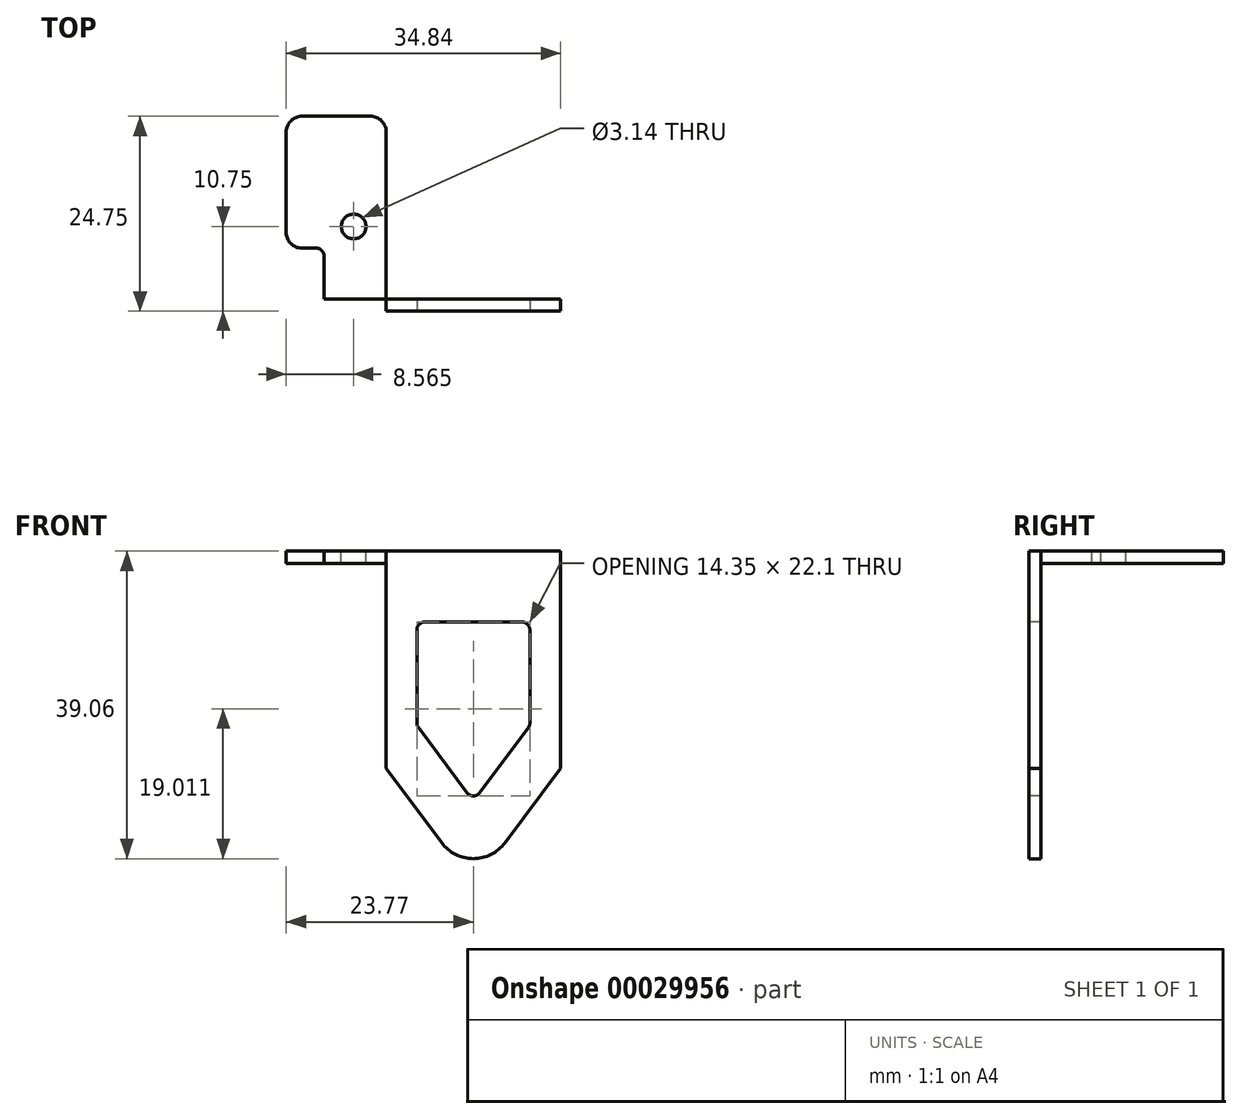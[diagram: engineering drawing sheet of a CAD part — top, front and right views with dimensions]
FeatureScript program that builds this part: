
annotation { "Feature Type Name" : "Feature", "Feature Type Description" : "" }
export const myFeature = defineFeature(function(context is Context, id is Id, definition is map)
    precondition{}
    {
        {
            var Q0;
            Q0=qCreatedBy(makeId("Top.planeOp"),FACE);
            var sketch = newSketch(context, id + "F0", { "sketchPlane" : qUnion([Q0])});
            skCircle(sketch, "E0", {"center": v(-15.2, 0) * mm, "radius": 1.57 * mm});
            skLineSegment(sketch, "E1", {"start": v(-15.2, 0) * mm, "end": v(0, 0) * mm, "construction": true});
            skLineSegment(sketch, "E2", {"start": v(0, 0) * mm, "end": v(15.2, 0) * mm, "construction": true});
            skLineSegment(sketch, "E3.bottom", {"start": v(-21.77, 14) * mm, "end": v(-13.07, 14) * mm});
            skLineSegment(sketch, "E3.top", {"start": v(-18.97, -10.75) * mm, "end": v(-11.07, -10.75) * mm});
            skLineSegment(sketch, "E3.left", {"start": v(-23.77, 12) * mm, "end": v(-23.77, -0.75) * mm});
            skLineSegment(sketch, "E3.right", {"start": v(-11.07, 12) * mm, "end": v(-11.07, -10.75) * mm});
            skLineSegment(sketch, "E4", {"start": v(-21.77, -2.75) * mm, "end": v(-19.97, -2.75) * mm});
            skLineSegment(sketch, "E5", {"start": v(-18.97, -3.75) * mm, "end": v(-18.97, -10.75) * mm});
            skPoint(sketch, "E6.visualSharp", {"position": v(-23.77, 14) * mm});
            skArc(sketch, "E6.filletArc", {"start": v(-21.77, 14) * mm, "mid": v(-23.18, 13.41) * mm, "end": v(-23.77, 12) * mm});
            skPoint(sketch, "E7.visualSharp", {"position": v(-11.07, 14) * mm});
            skArc(sketch, "E7.filletArc", {"start": v(-11.07, 12) * mm, "mid": v(-11.66, 13.41) * mm, "end": v(-13.07, 14) * mm});
            skPoint(sketch, "E8.visualSharp", {"position": v(-23.77, -2.75) * mm});
            skArc(sketch, "E8.filletArc", {"start": v(-23.77, -0.75) * mm, "mid": v(-23.18, -2.16) * mm, "end": v(-21.77, -2.75) * mm});
            skPoint(sketch, "E9.visualSharp", {"position": v(-18.97, -2.75) * mm});
            skArc(sketch, "E9.filletArc", {"start": v(-18.97, -3.75) * mm, "mid": v(-19.26, -3.04) * mm, "end": v(-19.97, -2.75) * mm});
            skLineSegment(sketch, "E10", {"start": v(0, 0) * mm, "end": v(0, -9.93) * mm, "construction": true});
            skArc(sketch, "E11.MirrorCS", {"start": v(18.97, -3.75) * mm, "mid": v(19.26, -3.04) * mm, "end": v(19.97, -2.75) * mm});
            skArc(sketch, "E12.MirrorCS", {"start": v(23.77, -0.75) * mm, "mid": v(23.18, -2.16) * mm, "end": v(21.77, -2.75) * mm});
            skCircle(sketch, "E13.MirrorC", {"center": v(15.2, 0) * mm, "radius": 1.57 * mm});
            skPoint(sketch, "E14.MirrorP", {"position": v(11.07, 14) * mm});
            skPoint(sketch, "E15.MirrorP", {"position": v(18.97, -2.75) * mm});
            skLineSegment(sketch, "E16.MirrorCS", {"start": v(18.97, -10.75) * mm, "end": v(11.07, -10.75) * mm});
            skLineSegment(sketch, "E17.MirrorCS", {"start": v(23.77, 12) * mm, "end": v(23.77, -0.75) * mm});
            skLineSegment(sketch, "E18.MirrorCS", {"start": v(21.77, -2.75) * mm, "end": v(19.97, -2.75) * mm});
            skLineSegment(sketch, "E19.MirrorCS", {"start": v(11.07, 12) * mm, "end": v(11.07, -10.75) * mm});
            skPoint(sketch, "E20.MirrorP", {"position": v(23.77, -2.75) * mm});
            skPoint(sketch, "E21.MirrorP", {"position": v(23.77, 14) * mm});
            skLineSegment(sketch, "E22.MirrorCS", {"start": v(18.97, -3.75) * mm, "end": v(18.97, -10.75) * mm});
            skArc(sketch, "E23.MirrorCS", {"start": v(21.77, 14) * mm, "mid": v(23.18, 13.41) * mm, "end": v(23.77, 12) * mm});
            skArc(sketch, "E24.MirrorCS", {"start": v(11.07, 12) * mm, "mid": v(11.66, 13.41) * mm, "end": v(13.07, 14) * mm});
            skLineSegment(sketch, "E25.MirrorCS", {"start": v(21.77, 14) * mm, "end": v(13.07, 14) * mm});
            skLineSegment(sketch, "E26.bottom", {"start": v(-18.97, -10.75) * mm, "end": v(18.97, -10.75) * mm});
            skLineSegment(sketch, "E26.top", {"start": v(-18.97, -9.2) * mm, "end": v(18.97, -9.2) * mm});
            skLineSegment(sketch, "E26.left", {"start": v(-18.97, -10.75) * mm, "end": v(-18.97, -9.2) * mm});
            skLineSegment(sketch, "E26.right", {"start": v(18.97, -10.75) * mm, "end": v(18.97, -9.2) * mm});
            skSolve(sketch);
        }
        {
            var Q0;
            Q0=makeQuery(id+"F0.imprint","IMPRINT",FACE,{"disambiguationData":[TD([[makeQuery(id+"F0.imprint","IMPRINT",EDGE,{"derivedFrom":sQuery(id+"F0.wireOp",EDGE,"E0")}),-1.0]])]});
            var Q1;
            Q1=makeQuery(id+"F0.imprint","IMPRINT",FACE,{"disambiguationData":[TD([[makeQuery(id+"F0.imprint","IMPRINT",EDGE,{"derivedFrom":sQuery(id+"F0.wireOp",EDGE,"E11.MirrorCS")}),1.0]])]});
            var Q2;
            {var subQ0=sQuery(id+"F0.wireOp",EDGE,"E26.left");Q2=makeQuery(id+"F0.imprint","IMPRINT",FACE,{"disambiguationData":[TD([[makeQuery(id+"F0.imprint","IMPRINT",EDGE,{"derivedFrom":subQ0}),-1.0]])]});}
            var Q3;
            {var subQ0=sQuery(id+"F0.wireOp",EDGE,"E26.right");Q3=makeQuery(id+"F0.imprint","IMPRINT",FACE,{"disambiguationData":[TD([[makeQuery(id+"F0.imprint","IMPRINT",EDGE,{"derivedFrom":subQ0}),1.0]])]});}
            extrude(context, id + "F1", {"entities" : qUnion([Q0, Q1, Q2, Q3]), "oppositeDirection" : true, "depth" : 1.55 * mm});
        }
        {
            var Q0;
            {var subQ0=sQuery(id+"F0.wireOp",EDGE,"E26.left");Q0=makeQuery(id+"F0.imprint","IMPRINT",FACE,{"disambiguationData":[TD([[makeQuery(id+"F0.imprint","IMPRINT",EDGE,{"derivedFrom":subQ0}),-1.0]])]});}
            var Q1;
            {var subQ3=sQuery(id+"F0.wireOp",EDGE,"E3.right");var subQ5=sQuery(id+"F0.wireOp",EDGE,"E26.bottom");var subQ7=makeQuery(id+"F0.imprint","INTERSECT",VERTEX,{"derivedFrom":[subQ3,subQ5]});Q1=makeQuery(id+"F0.imprint","IMPRINT",FACE,{"disambiguationData":[TD([[makeQuery(id+"F0.imprint","IMPRINT",EDGE,{"disambiguationData":[TD([[subQ7,1.0]])],"derivedFrom":subQ3}),1.0]])]});}
            var Q2;
            {var subQ0=sQuery(id+"F0.wireOp",EDGE,"E26.right");Q2=makeQuery(id+"F0.imprint","IMPRINT",FACE,{"disambiguationData":[TD([[makeQuery(id+"F0.imprint","IMPRINT",EDGE,{"derivedFrom":subQ0}),1.0]])]});}
            extrude(context, id + "F2", {"entities" : qUnion([Q0, Q1, Q2]), "operationType" : NewBodyOperationType.ADD, "oppositeDirection" : true, "depth" : 39.06 * mm});
        }
        {
            var Q0;
            {var subQ0=sQuery(id+"F0.wireOp",EDGE,"E26.bottom");Q0=makeQuery(id+"F2.boolean.opBoolean","MERGE",FACE,{"derivedFrom":[makeQuery(id+"F1.opExtrude","SWEPT_FACE",FACE,{"disambiguationData":[OSD([subQ0]),TDD([makeQuery(id+"F0.imprint","IMPRINT",EDGE,{"disambiguationData":[TD([[makeQuery(id+"F0.imprint","INTERSECT",VERTEX,{"derivedFrom":[sQuery(id+"F0.wireOp",EDGE,"E3.right"),subQ0]}),1.0]])],"derivedFrom":subQ0})])]}),makeQuery(id+"F1.opExtrude","SWEPT_FACE",FACE,{"disambiguationData":[OSD([subQ0]),TDD([makeQuery(id+"F0.imprint","IMPRINT",EDGE,{"disambiguationData":[TD([[makeQuery(id+"F0.imprint","INTERSECT",VERTEX,{"derivedFrom":[sQuery(id+"F0.wireOp",EDGE,"E19.MirrorCS"),subQ0]}),-1.0]])],"derivedFrom":subQ0})])]}),makeQuery(id+"F2.opExtrude","SWEPT_FACE",FACE,{"disambiguationData":[OSD([subQ0])]})]});}
            var sketch = newSketch(context, id + "F3", { "sketchPlane" : qUnion([Q0])});
            skLineSegment(sketch, "E27", {"start": v(-18.97, -17) * mm, "end": v(18.97, -17) * mm, "construction": true});
            skLineSegment(sketch, "E28", {"start": v(-18.97, -17) * mm, "end": v(-4, -37.05) * mm});
            skLineSegment(sketch, "E29", {"start": v(18.97, -17) * mm, "end": v(4, -37.05) * mm});
            skArc(sketch, "E30", {"start": v(-4, -37.05) * mm, "mid": v(0, -39.06) * mm, "end": v(4, -37.05) * mm});
            skLineSegment(sketch, "E31", {"start": v(-18.97, -17) * mm, "end": v(-18.97, -40.94) * mm});
            skLineSegment(sketch, "E32", {"start": v(-18.97, -40.94) * mm, "end": v(18.97, -40.94) * mm});
            skLineSegment(sketch, "E33", {"start": v(18.97, -40.94) * mm, "end": v(18.97, -17) * mm});
            skLineSegment(sketch, "E34", {"start": v(-6.18, -9) * mm, "end": v(6.18, -9) * mm});
            skLineSegment(sketch, "E35", {"start": v(7.18, -10) * mm, "end": v(7.18, -21.82) * mm});
            skLineSegment(sketch, "E36", {"start": v(6.98, -22.42) * mm, "end": v(0.8, -30.7) * mm});
            skLineSegment(sketch, "E37", {"start": v(-0.8, -30.7) * mm, "end": v(-6.98, -22.42) * mm});
            skLineSegment(sketch, "E38", {"start": v(-7.18, -21.82) * mm, "end": v(-7.18, -10) * mm});
            skPoint(sketch, "E39.visualSharp", {"position": v(0, -31.77) * mm});
            skArc(sketch, "E39.filletArc", {"start": v(-0.8, -30.7) * mm, "mid": v(0, -31.1) * mm, "end": v(0.8, -30.7) * mm});
            skPoint(sketch, "E40.visualSharp", {"position": v(-7.18, -22.15) * mm});
            skArc(sketch, "E40.filletArc", {"start": v(-7.18, -21.82) * mm, "mid": v(-7.13, -22.14) * mm, "end": v(-6.98, -22.42) * mm});
            skPoint(sketch, "E41.visualSharp", {"position": v(7.18, -22.15) * mm});
            skArc(sketch, "E41.filletArc", {"start": v(6.98, -22.42) * mm, "mid": v(7.13, -22.14) * mm, "end": v(7.18, -21.82) * mm});
            skPoint(sketch, "E42.visualSharp", {"position": v(7.18, -9) * mm});
            skArc(sketch, "E42.filletArc", {"start": v(7.18, -10) * mm, "mid": v(6.88, -9.3) * mm, "end": v(6.18, -9) * mm});
            skPoint(sketch, "E43.visualSharp", {"position": v(-7.18, -9) * mm});
            skArc(sketch, "E43.filletArc", {"start": v(-6.18, -9) * mm, "mid": v(-6.88, -9.3) * mm, "end": v(-7.18, -10) * mm});
            skSolve(sketch);
        }
        {
            var Q0;
            {var subQ7=sQuery(id+"F3.wireOp",EDGE,"E28");Q0=makeQuery(id+"F3.imprint","IMPRINT",FACE,{"disambiguationData":[TD([[makeQuery(id+"F3.imprint","IMPRINT",EDGE,{"derivedFrom":subQ7}),-1.0]])]});}
            var Q1;
            {var subQ7=sQuery(id+"F3.wireOp",EDGE,"E29");Q1=makeQuery(id+"F3.imprint","IMPRINT",FACE,{"disambiguationData":[TD([[makeQuery(id+"F3.imprint","IMPRINT",EDGE,{"derivedFrom":subQ7}),1.0]])]});}
            var Q2;
            {var subQ6=sQuery(id+"F3.wireOp",EDGE,"E32");Q2=makeQuery(id+"F3.imprint","IMPRINT",FACE,{"disambiguationData":[TD([[makeQuery(id+"F3.imprint","IMPRINT",EDGE,{"derivedFrom":subQ6}),1.0]])]});}
            extrude(context, id + "F4", {"entities" : qUnion([Q0, Q1, Q2]), "operationType" : NewBodyOperationType.REMOVE, "endBound" : BoundingType.THROUGH_ALL, "oppositeDirection" : true, "depth" : 25 * mm});
        }
        {
            var Q0;
            Q0=makeQuery(id+"F3.imprint","IMPRINT",FACE,{"disambiguationData":[TD([[makeQuery(id+"F3.imprint","IMPRINT",EDGE,{"derivedFrom":sQuery(id+"F3.wireOp",EDGE,"E34")}),-1.0]])]});
            extrude(context, id + "F5", {"entities" : qUnion([Q0]), "operationType" : NewBodyOperationType.REMOVE, "endBound" : BoundingType.THROUGH_ALL, "oppositeDirection" : true, "depth" : 25 * mm});
        }
    });
